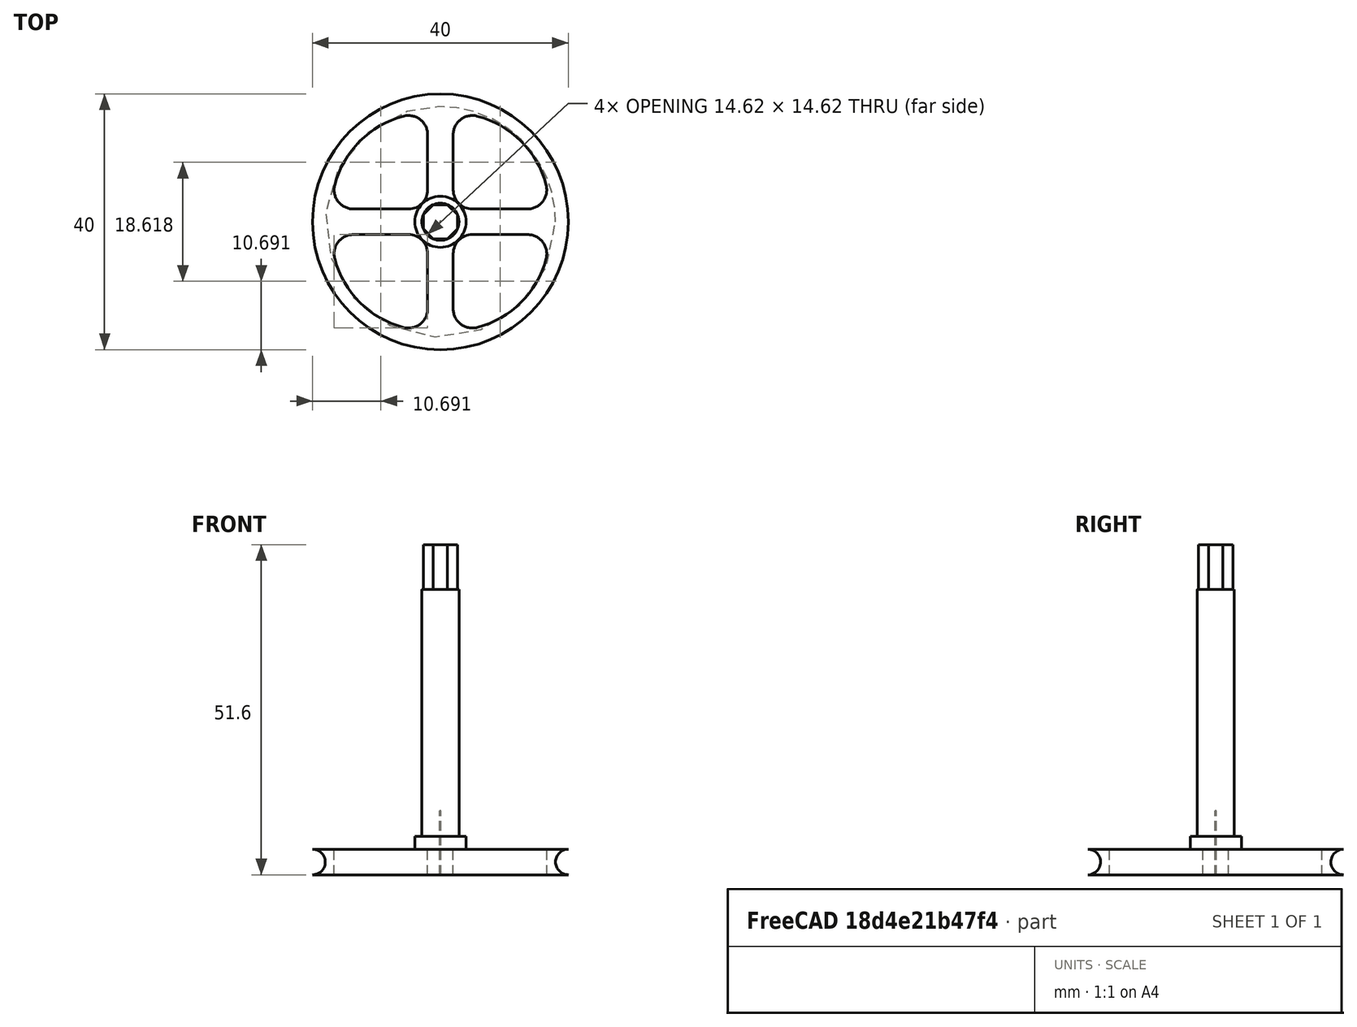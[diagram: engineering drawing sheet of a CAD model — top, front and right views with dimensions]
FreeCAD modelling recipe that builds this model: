
FCSTD DOCUMENT  (FreeCAD 0.18.1R)
Label: wheel right rear techdraw
License: All rights reserved
LicenseURL: http://en.wikipedia.org/wiki/All_rights_reserved
objects: TechDraw::DrawViewDimension×6, Part::Cylinder×4, PartDesign::Plane×4, TechDraw::DrawProjGroupItem×4, PartDesign::FeatureBase×3, Sketcher::SketchObject×3, PartDesign::Fillet×3, PartDesign::Body×3, PartDesign::Pocket×2, Part::Torus×1, Part::Cut×1, App::MeasureDistance×1, Part::MultiFuse×1, PartDesign::Pad×1, TechDraw::DrawSVGTemplate×1, TechDraw::DrawProjGroup×1, TechDraw::DrawPage×1
note: 29 computed .brp shape members not serialized (recipe doc carries the construction recipe); baked Part::Feature solids carry a one-line shape summary decoded from their .brp

FEATURE [Part::Cylinder] Cylinder
  Angle = 360
  AttacherType = Attacher::AttachEngine3D
  Height = 4
  Radius = 20
FEATURE [Part::Cylinder] Cylinder001
  Angle = 360
  AttacherType = Attacher::AttachEngine3D
  Height = 10
  Radius = 0.1
FEATURE [PartDesign::FeatureBase] BaseFeature
  BaseFeature = -> Cylinder
FEATURE [PartDesign::Plane] DatumPlane
  Length = 47.9863
  MapMode = 5
  Placement = pos=(0,0,0) rot=(1,0,0;3.14159rad)
  ResizeMode = 0
  Support = -> [BaseFeature]
  Width = 47.8497
FEATURE [Sketcher::SketchObject] Sketch001
  MapMode = 5
  Placement = pos=(0,0,0) rot=(1,0,0;3.14159rad)
  Support = -> [DatumPlane]
  sketch-geometry (12):
    g0: LineSegment StartX=2 StartY=17 StartZ=0 EndX=2 EndY=2 EndZ=0
    g1: LineSegment StartX=-2 StartY=17 StartZ=0 EndX=-2 EndY=2 EndZ=0
    g2: LineSegment StartX=2 StartY=2 StartZ=0 EndX=17 EndY=2 EndZ=0
    g3: LineSegment StartX=2 StartY=-2 StartZ=0 EndX=17 EndY=-2 EndZ=0
    g4: LineSegment StartX=-2 StartY=-2 StartZ=0 EndX=-2 EndY=-17 EndZ=0
    g5: LineSegment StartX=-17 StartY=-2 StartZ=0 EndX=-2 EndY=-2 EndZ=0
    g6: LineSegment StartX=-17 StartY=2 StartZ=0 EndX=-2 EndY=2 EndZ=0
    g7: LineSegment StartX=2 StartY=-2 StartZ=0 EndX=2 EndY=-17 EndZ=0
    g8: ArcOfCircle CenterX=2 CenterY=2 CenterZ=0 NormalX=0 NormalY=0 NormalZ=1 AngleXU=0 Radius=15 StartAngle=0 EndAngle=1.5708
    g9: ArcOfCircle CenterX=-2 CenterY=2 CenterZ=0 NormalX=0 NormalY=0 NormalZ=1 AngleXU=0 Radius=15 StartAngle=1.5708 EndAngle=3.14159
    g10: ArcOfCircle CenterX=-2 CenterY=-2 CenterZ=0 NormalX=0 NormalY=0 NormalZ=1 AngleXU=0 Radius=15 StartAngle=3.14159 EndAngle=4.71239
    g11: ArcOfCircle CenterX=2 CenterY=-2 CenterZ=0 NormalX=0 NormalY=0 NormalZ=1 AngleXU=0 Radius=15 StartAngle=4.71239 EndAngle=6.28319
  constraints (35):
    c: Vertical(g0)
    c: Vertical(g1)
    c: Horizontal(g2)
    c: Horizontal(g3)
    c: Vertical(g4)
    c: Horizontal(g6)
    c: DistanceX(g0) = 2
    c: DistanceY(g0) = 17
    c: DistanceY(g0) = 2
    c: Coincident(g0,g2)
    c: DistanceX(g3) = 2
    c: Coincident(g3,g7)
    c: DistanceX(g3) = 17
    c: DistanceY(g7) = -17
    c: DistanceX(g5) = -2
    c: DistanceY(g5) = -2
    c: Coincident(g5,g4)
    c: DistanceY(g4) = -17
    c: DistanceX(g5) = -17
    c: DistanceX(g6) = -2
    c: DistanceX(g6) = -17
    c: DistanceY(g6) = 2
    c: Coincident(g6,g1)
    c: Coincident(g8,g0)
    c: Coincident(g8,g0)
    c: Coincident(g9,g1)
    c: Coincident(g9,g1)
    c: Coincident(g9,g6)
    c: Coincident(g10,g4)
    c: Coincident(g10,g4)
    c: Coincident(g10,g5)
    c: Coincident(g11,g3)
    c: Coincident(g11,g3)
    c: Coincident(g11,g7)
    c: Coincident(g8,g2)
FEATURE [PartDesign::Pocket] Pocket
  BaseFeature = -> BaseFeature
  Length = 5
  Length2 = 100
  Profile = -> Sketch001
  Type = 1
FEATURE [PartDesign::Fillet] Fillet
  Base = -> Pocket [Edge39]
  BaseFeature = -> Pocket
  Radius = 3
FEATURE [PartDesign::Fillet] Fillet001
  Base = -> Fillet [Edge27,Edge39,Edge41,Edge17,Edge26,Edge32,Edge35]
  BaseFeature = -> Fillet
  Radius = 3
FEATURE [PartDesign::Fillet] Fillet002
  Base = -> Fillet001 [Edge56,Edge46,Edge42,Edge30]
  BaseFeature = -> Fillet001
  Radius = 3
FEATURE [PartDesign::Body] Body
  BaseFeature = -> Cylinder
  Group = -> [BaseFeature,DatumPlane,Sketch001,Pocket,Fillet,Fillet001,Fillet002]
  Origin = -> Origin
  Tip = -> Fillet002
FEATURE [Part::Torus] Torus
  Angle1 = -180
  Angle2 = 180
  Angle3 = 360
  AttacherType = Attacher::AttachEngine3D
  Placement = pos=(0,0,2) rot=(0,0,1;0rad)
  Radius1 = 20
  Radius2 = 2
FEATURE [Part::Cut] Cut
  Base = -> Body
  Tool = -> Torus
FEATURE [PartDesign::FeatureBase] BaseFeature001
  BaseFeature = -> Cut
FEATURE [PartDesign::Plane] DatumPlane001
  Length = 48
  MapMode = 5
  Placement = pos=(0,0,0) rot=(1,0,0;3.14159rad)
  ResizeMode = 0
  Support = -> [BaseFeature001]
  Width = 48
FEATURE [PartDesign::Plane] DatumPlane002
  Length = 48
  MapMode = 5
  Placement = pos=(0,0,0) rot=(1,0,0;3.14159rad)
  ResizeMode = 0
  Support = -> [BaseFeature001]
  Width = 48
FEATURE [Sketcher::SketchObject] Sketch
  MapMode = 5
  Placement = pos=(0,0,0) rot=(1,0,0;3.14159rad)
  Support = -> [DatumPlane002]
  sketch-geometry (9):
    g0: LineSegment StartX=1.10978 StartY=-2.67925 StartZ=0 EndX=2.67925 EndY=-1.10978 EndZ=0
    g1: LineSegment StartX=2.67925 StartY=-1.10978 StartZ=0 EndX=2.67925 EndY=1.10978 EndZ=0
    g2: LineSegment StartX=2.67925 StartY=1.10978 StartZ=0 EndX=1.10978 EndY=2.67925 EndZ=0
    g3: LineSegment StartX=1.10978 StartY=2.67925 StartZ=0 EndX=-1.10978 EndY=2.67925 EndZ=0
    g4: LineSegment StartX=-1.10978 StartY=2.67925 StartZ=0 EndX=-2.67925 EndY=1.10978 EndZ=0
    g5: LineSegment StartX=-2.67925 StartY=1.10978 StartZ=0 EndX=-2.67925 EndY=-1.10978 EndZ=0
    g6: LineSegment StartX=-2.67925 StartY=-1.10978 StartZ=0 EndX=-1.10978 EndY=-2.67925 EndZ=0
    g7: LineSegment StartX=-1.10978 StartY=-2.67925 StartZ=0 EndX=1.10978 EndY=-2.67925 EndZ=0
    g8: Circle [constr] CenterX=0 CenterY=0 CenterZ=0 NormalX=0 NormalY=0 NormalZ=1 AngleXU=0 Radius=2.9
  constraints (20):
    c: Coincident(g0,g1)
    c: Coincident(g1,g2)
    c: Coincident(g2,g3)
    c: Coincident(g3,g4)
    c: Coincident(g4,g5)
    c: Coincident(g5,g6)
    c: Coincident(g6,g7)
    c: Coincident(g7,g0)
    c: Equal(g0, g1-g7) x7
    c: PointOnObject(g0,g8)
    c: PointOnObject(g1,g8)
    c: PointOnObject(g2,g8)
    c: PointOnObject(g3,g8)
    c: PointOnObject(g4,g8)
    c: PointOnObject(g5,g8)
    c: PointOnObject(g6,g8)
    c: PointOnObject(g7,g8)
    c: Coincident(g8,g-1)
    c: Radius(g8) = 2.9
    c: DistanceX(g1,g0) = 0
FEATURE [PartDesign::Pocket] Pocket001
  BaseFeature = -> BaseFeature001
  Length = 5
  Length2 = 100
  Profile = -> Sketch
  Type = 0
FEATURE [PartDesign::Body] Body001
  BaseFeature = -> Cut
  Group = -> [BaseFeature001,DatumPlane001,DatumPlane002,Sketch,Pocket001]
  Origin = -> Origin001
  Tip = -> Pocket001
FEATURE [Part::Cylinder] Cylinder002
  Angle = 360
  AttacherType = Attacher::AttachEngine3D
  Height = 44.6
  Radius = 2.9
FEATURE [App::MeasureDistance] Distance  label="Distance: 4.03 mm"
  Distance = 4.03426
  P1 = (-19.6792,-3.42447,0)
  P2 = (-19.7612,-2.90625,4)
FEATURE [Part::Cylinder] Cylinder003
  Angle = 360
  AttacherType = Attacher::AttachEngine3D
  Height = 6
  Radius = 4
FEATURE [Part::MultiFuse] Fusion
  Shapes = -> [Body001,Cylinder002,Cylinder003]
FEATURE [PartDesign::FeatureBase] BaseFeature002
  BaseFeature = -> Fusion
FEATURE [PartDesign::Plane] DatumPlane003
  Length = 47.9907
  MapMode = 5
  Placement = pos=(0,0,44.6) rot=(0,0,1;0rad)
  ResizeMode = 0
  Support = -> [BaseFeature002]
  Width = 47.8974
FEATURE [Sketcher::SketchObject] Sketch002
  MapMode = 5
  Placement = pos=(0,0,44.6) rot=(0,0,1;0rad)
  Support = -> [DatumPlane003]
  sketch-geometry (9):
    g0: LineSegment StartX=2.67925 StartY=1.10978 StartZ=0 EndX=1.10978 EndY=2.67925 EndZ=0
    g1: LineSegment StartX=1.10978 StartY=2.67925 StartZ=0 EndX=-1.10978 EndY=2.67925 EndZ=0
    g2: LineSegment StartX=-1.10978 StartY=2.67925 StartZ=0 EndX=-2.67925 EndY=1.10978 EndZ=0
    g3: LineSegment StartX=-2.67925 StartY=1.10978 StartZ=0 EndX=-2.67925 EndY=-1.10978 EndZ=0
    g4: LineSegment StartX=-2.67925 StartY=-1.10978 StartZ=0 EndX=-1.10978 EndY=-2.67925 EndZ=0
    g5: LineSegment StartX=-1.10978 StartY=-2.67925 StartZ=0 EndX=1.10978 EndY=-2.67925 EndZ=0
    g6: LineSegment StartX=1.10978 StartY=-2.67925 StartZ=0 EndX=2.67925 EndY=-1.10978 EndZ=0
    g7: LineSegment StartX=2.67925 StartY=-1.10978 StartZ=0 EndX=2.67925 EndY=1.10978 EndZ=0
    g8: Circle [constr] CenterX=0 CenterY=0 CenterZ=0 NormalX=0 NormalY=0 NormalZ=1 AngleXU=0 Radius=2.9
  constraints (20):
    c: Coincident(g0,g1)
    c: Coincident(g1,g2)
    c: Coincident(g2,g3)
    c: Coincident(g3,g4)
    c: Coincident(g4,g5)
    c: Coincident(g5,g6)
    c: Coincident(g6,g7)
    c: Coincident(g7,g0)
    c: Equal(g0, g1-g7) x7
    c: PointOnObject(g0,g8)
    c: PointOnObject(g1,g8)
    c: PointOnObject(g2,g8)
    c: PointOnObject(g3,g8)
    c: PointOnObject(g4,g8)
    c: PointOnObject(g5,g8)
    c: PointOnObject(g6,g8)
    c: PointOnObject(g7,g8)
    c: Radius(g8) = 2.9
    c: Coincident(g-1,g8)
    c: DistanceX(g0,g6) = 0
FEATURE [PartDesign::Pad] Pad
  BaseFeature = -> BaseFeature002
  Length = 7
  Length2 = 100
  Profile = -> Sketch002
  Type = 0
FEATURE [PartDesign::Body] Body002
  BaseFeature = -> Fusion
  Group = -> [BaseFeature002,DatumPlane003,Sketch002,Pad]
  Origin = -> Origin002
  Tip = -> Pad
FEATURE [TechDraw::DrawSVGTemplate] Template
  EditableTexts = Designed_by_Name=Designed by Name; Drawing_number=Drawing number; FC-Date=Date; FC-SC=Scale; FC-SH=Sheet; FC-Title=Title; Subtitle=Subtitle; Weight=Weight
  Height = 210
  Orientation = 1
  Width = 297
FEATURE [TechDraw::DrawProjGroupItem] ProjItem  label="Front"
  CoarseView = false
  Direction = (0,-1,0)
  Focus = 100
  HardHidden = false
  IsoCount = 0
  IsoHidden = false
  IsoVisible = false
  LockPosition = true
  Perspective = false
  Rotation = 0
  RotationVector = (1,0,0)
  ScaleType = 2
  SeamHidden = false
  SeamVisible = false
  SmoothHidden = false
  SmoothVisible = false
  Source = -> [Pad]
  Type = 0
  X = 0
  Y = 0
FEATURE [TechDraw::DrawProjGroupItem] ProjItem001  label="Left"
  CoarseView = false
  Direction = (-1,-1e-16,0)
  Focus = 100
  HardHidden = false
  IsoCount = 0
  IsoHidden = false
  IsoVisible = false
  LockPosition = false
  Perspective = false
  Rotation = 0
  RotationVector = (1e-16,-1,0)
  ScaleType = 2
  SeamHidden = false
  SeamVisible = false
  SmoothHidden = false
  SmoothVisible = false
  Source = -> [Pad]
  Type = 1
  X = 70.2251
  Y = 0
FEATURE [TechDraw::DrawProjGroupItem] ProjItem002  label="FrontTopLeft"
  CoarseView = false
  Direction = (-1,-1,1)
  Focus = 100
  HardHidden = false
  IsoCount = 0
  IsoHidden = false
  IsoVisible = false
  LockPosition = false
  Perspective = false
  Rotation = 0
  RotationVector = (1,-1,0)
  ScaleType = 2
  SeamHidden = false
  SeamVisible = false
  SmoothHidden = false
  SmoothVisible = false
  Source = -> [Pad]
  Type = 6
  X = 70.2251
  Y = -70.2251
FEATURE [TechDraw::DrawProjGroupItem] ProjItem003  label="Top"
  CoarseView = false
  Direction = (0,0,1)
  Focus = 100
  HardHidden = false
  IsoCount = 0
  IsoHidden = false
  IsoVisible = false
  LockPosition = false
  Perspective = false
  Rotation = 0
  RotationVector = (1,0,0)
  ScaleType = 2
  SeamHidden = false
  SeamVisible = false
  SmoothHidden = false
  SmoothVisible = false
  Source = -> [Pad]
  Type = 4
  X = 0
  Y = -70.2251
FEATURE [TechDraw::DrawProjGroup] ProjGroup
  Anchor = -> ProjItem
  AutoDistribute = true
  LockPosition = false
  ProjectionType = 0
  Rotation = 0
  ScaleType = 0
  Source = -> [Pad]
  Views = -> [ProjItem,ProjItem001,ProjItem002,ProjItem003]
  X = 68.089
  Y = 158.552
  spacingX = 15
  spacingY = 15
FEATURE [TechDraw::DrawViewDimension] Dimension
  Arbitrary = false
  FormatSpec = %.2f
  LockPosition = false
  MeasureType = 1
  OverTolerance = 0
  References2D = -> [ProjItem]
  Rotation = 0
  ScaleType = 0
  Type = 2
  UnderTolerance = 0
  X = 10.0962
  Y = -1.18535
FEATURE [TechDraw::DrawViewDimension] Dimension001
  Arbitrary = false
  FormatSpec = %.2f
  LockPosition = false
  MeasureType = 1
  OverTolerance = 0
  References2D = -> [ProjItem]
  Rotation = 0
  ScaleType = 0
  Type = 2
  UnderTolerance = 0
  X = 18.0372
  Y = 25.759
FEATURE [TechDraw::DrawViewDimension] Dimension002
  Arbitrary = false
  FormatSpec = ⌀%.2f
  LockPosition = false
  MeasureType = 1
  OverTolerance = 0
  References2D = -> [ProjItem003]
  Rotation = 0
  ScaleType = 0
  Type = 5
  UnderTolerance = 0
  X = -10.2143
  Y = 30.2938
FEATURE [TechDraw::DrawViewDimension] Dimension003
  Arbitrary = false
  FormatSpec = R%.2f
  LockPosition = false
  MeasureType = 1
  OverTolerance = 0
  References2D = -> [ProjItem003]
  Rotation = 0
  ScaleType = 0
  Type = 4
  UnderTolerance = 0
  X = 25.3946
  Y = 25.4258
FEATURE [TechDraw::DrawViewDimension] Dimension004
  Arbitrary = false
  FormatSpec = %.2f
  LockPosition = false
  MeasureType = 1
  OverTolerance = 0
  References2D = -> [ProjItem003]
  Rotation = 0
  ScaleType = 0
  Type = 1
  UnderTolerance = 0
  X = -17.7439
  Y = 18.8689
FEATURE [TechDraw::DrawViewDimension] Dimension005
  Arbitrary = false
  FormatSpec = R%.2f
  LockPosition = false
  MeasureType = 1
  OverTolerance = 0
  References2D = -> [ProjItem003]
  Rotation = 0
  ScaleType = 0
  Type = 4
  UnderTolerance = 0
  X = -38.0162
  Y = -4.67659
FEATURE [TechDraw::DrawPage] Page
  KeepUpdated = true
  ProjectionType = 0
  Template = -> Template
  Views = -> [ProjGroup,Dimension,Dimension001,Dimension002,Dimension003,Dimension004,Dimension005]
